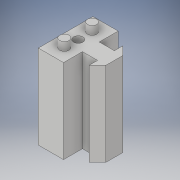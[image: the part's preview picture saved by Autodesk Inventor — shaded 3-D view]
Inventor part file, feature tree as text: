
AUTODESK INVENTOR PART (.ipt)
format: ipt  version: 2018 (Build 220112000, 112)  size: 130,048 bytes
history: native  units: in
note: dims shown in document units (in); Inventor stores cm internally (conversion verified against a paired STEP export)
features: sketch x3, extrude x2, hole x1
ambient origin geometry x8: Origin, YZ Plane, XZ Plane, XY Plane, X Axis, Y Axis, Z Axis, Center Point
bodies: Solid1 (feature_tree)
feature tree (6):
  extrude  "Extrusion1"  Depth=0.65in
  extrude  "Extrusion2"  Depth=0.28in
  hole  "Hole1"  [1 undecoded]
  sketch  "Sketch1"  dims[d0=0.3in d1=0.65in]
  sketch  "Sketch2"  dims[d2=0.225in d3=0.28in]
  sketch  "Sketch3"  dims[d4=0.2in d5=0.1in d6=0.1in d7=0.1in d8=1.0in d9=0.0in d10=0.16in d11=0.16in d12=0.11in d13=0.11in d14=0.1in d15=0.0in d16=0.325in d17=0.11in d18=0.75in d19=0.375in d20=0.25in d21=0.5635in d22=0.45in d23=0.8108in]
note: 1 required parameter value undecoded (feature->parameter linkage not recoverable at this tier; creation-order binding heuristic only, values carry confidence <= 0.55)
